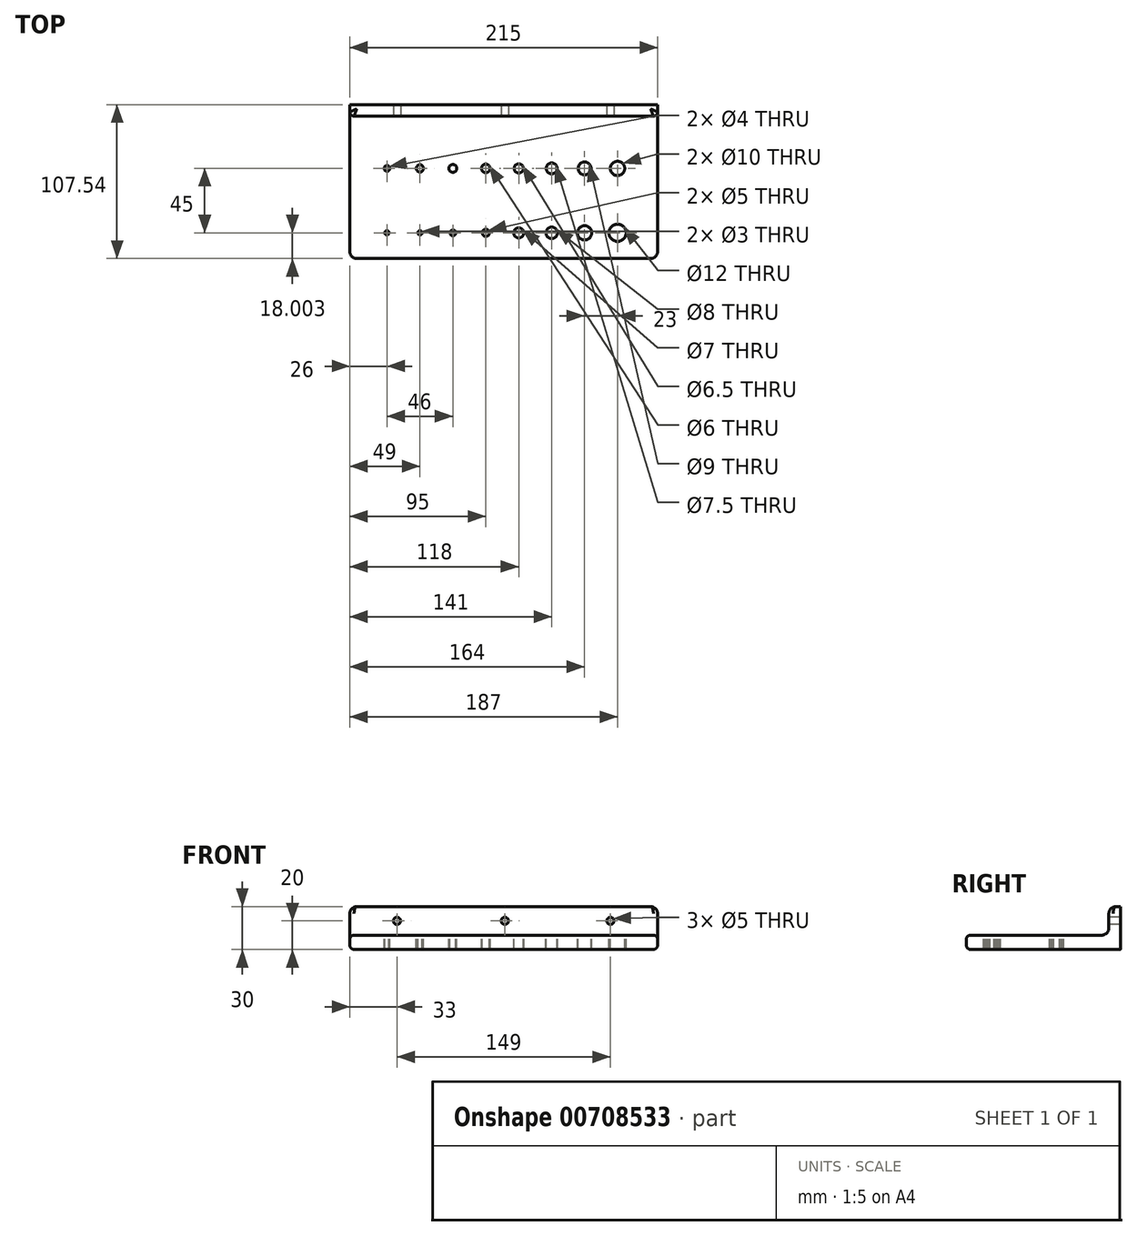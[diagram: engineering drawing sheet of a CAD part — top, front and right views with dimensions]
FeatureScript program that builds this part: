
annotation { "Feature Type Name" : "Feature", "Feature Type Description" : "" }
export const myFeature = defineFeature(function(context is Context, id is Id, definition is map)
    precondition{}
    {
        {
            var Q0;
            Q0=qCreatedBy(makeId("Top.planeOp"),FACE);
            var sketch = newSketch(context, id + "F0", { "sketchPlane" : qUnion([Q0])});
            skLineSegment(sketch, "E0.bottom", {"start": v(-108.54, 59.88) * mm, "end": v(106.46, 59.88) * mm});
            skLineSegment(sketch, "E0.top", {"start": v(-108.54, -40.12) * mm, "end": v(106.46, -40.12) * mm});
            skLineSegment(sketch, "E0.left", {"start": v(-108.54, 59.88) * mm, "end": v(-108.54, -40.12) * mm});
            skLineSegment(sketch, "E0.right", {"start": v(106.46, 59.88) * mm, "end": v(106.46, -40.12) * mm});
            skSolve(sketch);
        }
        {
            var Q0;
            Q0=makeQuery(id+"F0.imprint","IMPRINT",FACE,{"disambiguationData":[TD([[makeQuery(id+"F0.imprint","IMPRINT",EDGE,{"derivedFrom":sQuery(id+"F0.wireOp",EDGE,"E0.bottom")}),-1.0]])]});
            extrude(context, id + "F1", {"entities" : qUnion([Q0]), "depth" : 10 * mm, "offsetDistance" : 25 * mm});
        }
        {
            var Q0;
            Q0=qCreatedBy(makeId("Top.planeOp"),FACE);
            var sketch = newSketch(context, id + "F2", { "sketchPlane" : qUnion([Q0])});
            skLineSegment(sketch, "E1.bottom", {"start": v(-108.54, 59.42) * mm, "end": v(106.46, 59.42) * mm});
            skLineSegment(sketch, "E1.top", {"start": v(-108.54, 67.42) * mm, "end": v(106.46, 67.42) * mm});
            skLineSegment(sketch, "E1.left", {"start": v(-108.54, 59.42) * mm, "end": v(-108.54, 67.42) * mm});
            skLineSegment(sketch, "E1.right", {"start": v(106.46, 59.42) * mm, "end": v(106.46, 67.42) * mm});
            skSolve(sketch);
        }
        {
            var Q0;
            Q0 = qSketchRegion(id + "F2", true);
            extrude(context, id + "F3", {"entities" : qUnion([Q0]), "operationType" : NewBodyOperationType.ADD, "depth" : 30 * mm, "offsetDistance" : 25 * mm});
        }
        {
            var Q0;
            Q0=makeQuery(id+"F3.boolean.opBoolean","INTERSECT",EDGE,{"derivedFrom":[makeQuery(id+"F1.opExtrude","CAP_FACE",FACE,{"disambiguationData":[OSD([sQuery(id+"F0.wireOp",EDGE,"E0.bottom"),sQuery(id+"F0.wireOp",EDGE,"E0.top"),sQuery(id+"F0.wireOp",EDGE,"E0.left"),sQuery(id+"F0.wireOp",EDGE,"E0.right")])],"isStart":false}),makeQuery(id+"F3.opExtrude","SWEPT_FACE",FACE,{"disambiguationData":[OSD([sQuery(id+"F2.wireOp",EDGE,"E1.bottom")])]})]});
            fillet(context, id + "F4", {"entities" : qUnion([Q0]), "radius" : 5 * mm, "tangentPropagation" : true, "allowEdgeOverflow" : false});
        }
        {
            var Q0;
            Q0=makeQuery(id+"F1.opExtrude","CAP_EDGE",EDGE,{"disambiguationData":[OSD([sQuery(id+"F0.wireOp",EDGE,"E0.right")])],"isStart":false});
            var Q1;
            Q1=makeQuery(id+"F3.boolean.opBoolean","MERGE",EDGE,{"derivedFrom":[makeQuery(id+"F1.opExtrude","CAP_EDGE",EDGE,{"disambiguationData":[OSD([sQuery(id+"F0.wireOp",EDGE,"E0.right")])],"isStart":true}),makeQuery(id+"F3.opExtrude","CAP_EDGE",EDGE,{"disambiguationData":[OSD([sQuery(id+"F2.wireOp",EDGE,"E1.right")])],"isStart":true})]});
            var Q2;
            Q2=makeQuery(id+"F1.opExtrude","CAP_EDGE",EDGE,{"disambiguationData":[OSD([sQuery(id+"F0.wireOp",EDGE,"E0.top")])],"isStart":false});
            var Q3;
            Q3=makeQuery(id+"F1.opExtrude","CAP_EDGE",EDGE,{"disambiguationData":[OSD([sQuery(id+"F0.wireOp",EDGE,"E0.top")])],"isStart":true});
            var Q4;
            Q4=makeQuery(id+"F3.boolean.opBoolean","MERGE",EDGE,{"derivedFrom":[makeQuery(id+"F1.opExtrude","CAP_EDGE",EDGE,{"disambiguationData":[OSD([sQuery(id+"F0.wireOp",EDGE,"E0.left")])],"isStart":true}),makeQuery(id+"F3.opExtrude","CAP_EDGE",EDGE,{"disambiguationData":[OSD([sQuery(id+"F2.wireOp",EDGE,"E1.left")])],"isStart":true})]});
            var Q5;
            Q5=makeQuery(id+"F1.opExtrude","CAP_EDGE",EDGE,{"disambiguationData":[OSD([sQuery(id+"F0.wireOp",EDGE,"E0.left")])],"isStart":false});
            fillet(context, id + "F5", {"entities" : qUnion([Q0, Q1, Q2, Q3, Q4, Q5]), "radius" : 3 * mm, "tangentPropagation" : true, "allowEdgeOverflow" : false});
        }
        {
            var Q0;
            Q0=makeQuery(id+"F1.opExtrude","SWEPT_EDGE",EDGE,{"disambiguationData":[OSD([sQuery(id+"F0.wireOp",EDGE,"E0.top"),sQuery(id+"F0.wireOp",EDGE,"E0.left")])]});
            var Q1;
            Q1=makeQuery(id+"F1.opExtrude","SWEPT_EDGE",EDGE,{"disambiguationData":[OSD([sQuery(id+"F0.wireOp",EDGE,"E0.top"),sQuery(id+"F0.wireOp",EDGE,"E0.right")])]});
            fillet(context, id + "F6", {"entities" : qUnion([Q0, Q1]), "radius" : 5 * mm, "tangentPropagation" : true, "allowEdgeOverflow" : false});
        }
        {
            var Q0;
            Q0=makeQuery(id+"F1.opExtrude","CAP_FACE",FACE,{"disambiguationData":[OSD([sQuery(id+"F0.wireOp",EDGE,"E0.bottom"),sQuery(id+"F0.wireOp",EDGE,"E0.top"),sQuery(id+"F0.wireOp",EDGE,"E0.left"),sQuery(id+"F0.wireOp",EDGE,"E0.right")])],"isStart":false});
            var sketch = newSketch(context, id + "F7", { "sketchPlane" : qUnion([Q0])});
            skLineSegment(sketch, "E2", {"start": v(-105.54, -22.12) * mm, "end": v(103.46, -22.12) * mm, "construction": true});
            skLineSegment(sketch, "E3", {"start": v(-105.54, 22.88) * mm, "end": v(103.46, 22.88) * mm, "construction": true});
            skCircle(sketch, "E4", {"center": v(-82.54, 22.88) * mm, "radius": 2 * mm});
            skCircle(sketch, "E5", {"center": v(-59.54, 22.88) * mm, "radius": 2.5 * mm});
            skCircle(sketch, "E6", {"center": v(-13.54, 22.88) * mm, "radius": 3 * mm});
            skCircle(sketch, "E7", {"center": v(9.46, 22.88) * mm, "radius": 3.25 * mm});
            skCircle(sketch, "E8", {"center": v(-36.54, 22.88) * mm, "radius": 2.75 * mm});
            skCircle(sketch, "E9", {"center": v(32.46, 22.88) * mm, "radius": 3.75 * mm});
            skCircle(sketch, "E10", {"center": v(55.46, 22.88) * mm, "radius": 4.5 * mm});
            skCircle(sketch, "E11", {"center": v(78.46, 22.88) * mm, "radius": 5 * mm});
            skCircle(sketch, "E12", {"center": v(-82.54, -22.12) * mm, "radius": 1.5 * mm});
            skCircle(sketch, "E13", {"center": v(-59.54, -22.12) * mm, "radius": 1.5 * mm});
            skCircle(sketch, "E14", {"center": v(-36.54, -22.12) * mm, "radius": 2 * mm});
            skCircle(sketch, "E15", {"center": v(-13.54, -22.12) * mm, "radius": 2.5 * mm});
            skCircle(sketch, "E16", {"center": v(9.46, -22.12) * mm, "radius": 3.5 * mm});
            skCircle(sketch, "E17", {"center": v(32.46, -22.12) * mm, "radius": 4 * mm});
            skCircle(sketch, "E18", {"center": v(55.46, -22.12) * mm, "radius": 5 * mm});
            skCircle(sketch, "E19", {"center": v(78.46, -22.12) * mm, "radius": 6 * mm});
            skSolve(sketch);
        }
        {
            var Q0;
            Q0 = qSketchRegion(id + "F7", true);
            extrude(context, id + "F8", {"entities" : qUnion([Q0]), "operationType" : NewBodyOperationType.REMOVE, "oppositeDirection" : true, "depth" : 25 * mm, "offsetDistance" : 25 * mm});
        }
        {
            var Q0;
            Q0=makeQuery(id+"F3.opExtrude","CAP_EDGE",EDGE,{"disambiguationData":[OSD([sQuery(id+"F2.wireOp",EDGE,"E1.bottom")])],"isStart":false});
            fillet(context, id + "F9", {"entities" : qUnion([Q0]), "radius" : 5 * mm, "tangentPropagation" : true, "allowEdgeOverflow" : false});
        }
        {
            var Q0;
            Q0=makeQuery(id+"F3.opExtrude","SWEPT_FACE",FACE,{"disambiguationData":[OSD([sQuery(id+"F2.wireOp",EDGE,"E1.bottom")])]});
            var sketch = newSketch(context, id + "F10", { "sketchPlane" : qUnion([Q0])});
            skLineSegment(sketch, "E20", {"start": v(-105.54, 20) * mm, "end": v(129.46, 20) * mm, "construction": true});
            skCircle(sketch, "E21", {"center": v(-75.54, 20) * mm, "radius": 2.5 * mm});
            skCircle(sketch, "E22", {"center": v(11.96, 20) * mm, "radius": 2.5 * mm});
            skCircle(sketch, "E23", {"center": v(73.46, 20) * mm, "radius": 2.5 * mm});
            skSolve(sketch);
        }
        {
            var Q0;
            Q0=makeQuery(id+"F10.imprint","IMPRINT",FACE,{"disambiguationData":[TD([[makeQuery(id+"F10.imprint","IMPRINT",EDGE,{"derivedFrom":sQuery(id+"F10.wireOp",EDGE,"E21")}),1.0]])]});
            var Q1;
            Q1=makeQuery(id+"F10.imprint","IMPRINT",FACE,{"disambiguationData":[TD([[makeQuery(id+"F10.imprint","IMPRINT",EDGE,{"derivedFrom":sQuery(id+"F10.wireOp",EDGE,"E23")}),1.0]])]});
            extrude(context, id + "F11", {"entities" : qUnion([Q0, Q1]), "operationType" : NewBodyOperationType.REMOVE, "oppositeDirection" : true, "depth" : 25 * mm, "offsetDistance" : 25 * mm});
        }
        {
            var Q0;
            Q0=makeQuery(id+"F3.opExtrude","SWEPT_FACE",FACE,{"disambiguationData":[OSD([sQuery(id+"F2.wireOp",EDGE,"E1.bottom")])]});
            var sketch = newSketch(context, id + "F12", { "sketchPlane" : qUnion([Q0])});
            skCircle(sketch, "E24", {"center": v(-0.24, 20) * mm, "radius": 2.5 * mm});
            skLineSegment(sketch, "E25", {"start": v(-103.94, 20) * mm, "end": v(103.46, 20) * mm, "construction": true});
            skPoint(sketch, "E25.startSnap0", {"position": v(-105.54, 20) * mm});
            skSolve(sketch);
        }
        {
            var Q0;
            Q0 = qSketchRegion(id + "F12", true);
            extrude(context, id + "F13", {"entities" : qUnion([Q0]), "operationType" : NewBodyOperationType.REMOVE, "oppositeDirection" : true, "depth" : 25 * mm, "offsetDistance" : 25 * mm});
        }
    });
